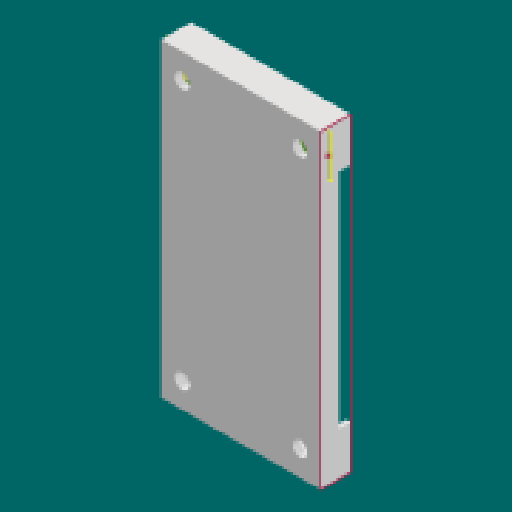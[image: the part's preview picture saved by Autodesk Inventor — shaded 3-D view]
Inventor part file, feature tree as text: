
AUTODESK INVENTOR PART (.ipt)
format: ipt  version: 2025.2 (Build 292293000, 293)  size: 129,536 bytes
history: native  units: mm
features: reference x7, sketch x4, extrude x3, other x2, plane x1
ambient origin geometry x8: Origin, YZ Plane, XZ Plane, XY Plane, X Axis, Y Axis, Z Axis, Center Point
bodies: Solid1 (feature_tree)
feature tree (17):
  plane  "Work Plane1"
  extrude  "Extrusion1"  Depth=203.0mm
  extrude  "Extrusion2"  Depth=5.0mm TaperAngle=0.0deg
  sketch  "Sketch3"  dims[d5=3.0mm d6=15.0mm d7=0.0mm]
  extrude  "Extrusion3"  Depth=15.0mm TaperAngle=0.0deg
  sketch  "Sketch1"  dims[d0=106.0mm d1=203.0mm]
  reference  "Reference1"
  reference  "Reference2"
  reference  "Reference3"
  reference  "Reference4"
  reference  "Reference5"
  sketch  "Sketch2"  dims[d2=3.0mm d3=5.0mm d4=0.0mm]
  sketch  "Sketch4"  dims[d8=15.0mm d9=0.0mm]
  reference  "Reference6"
  reference  "Reference7"
  other  "CassingHardware.iam"
  other  "atas:1"
